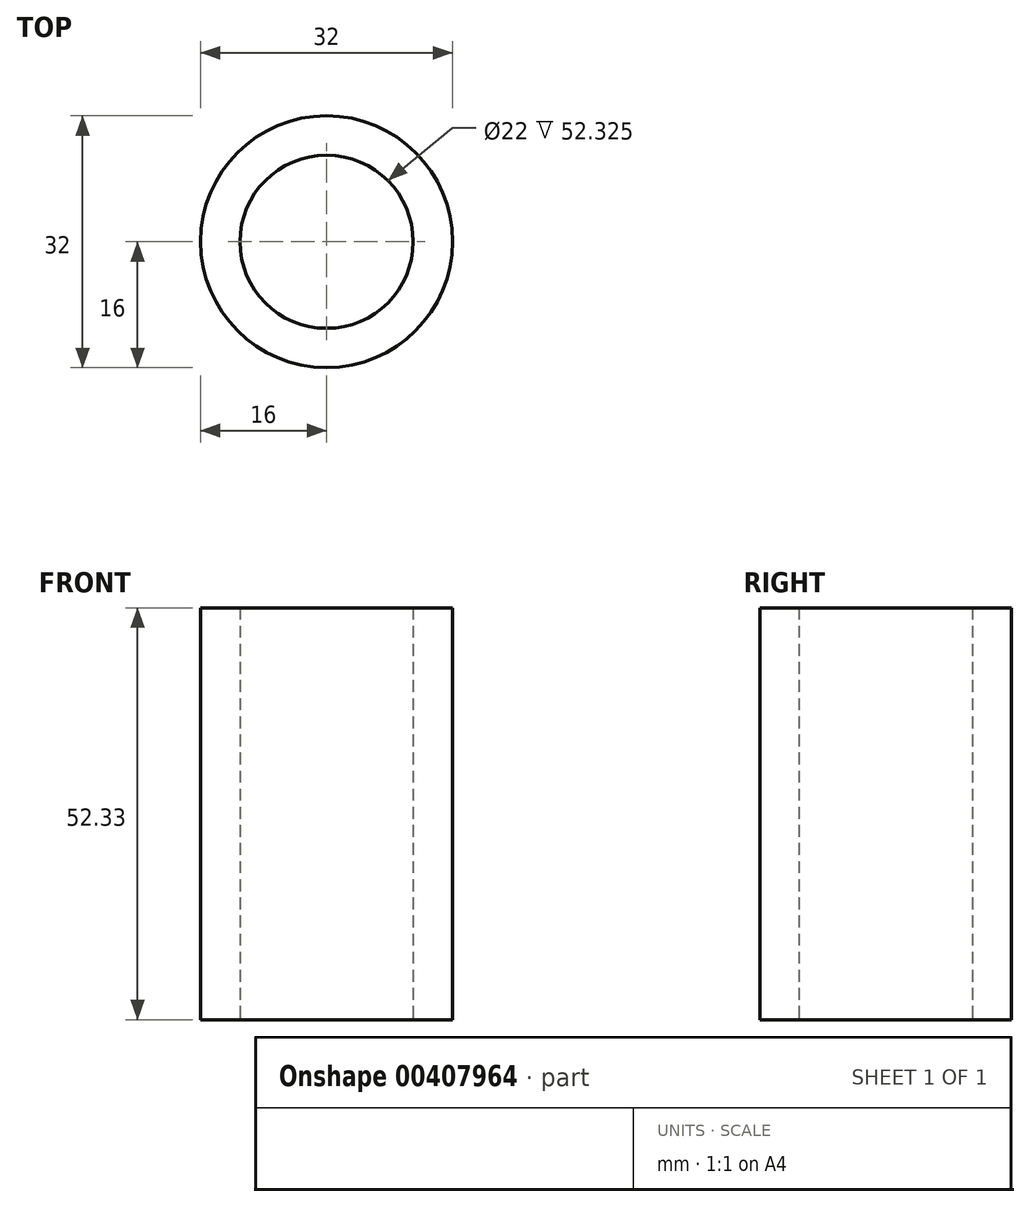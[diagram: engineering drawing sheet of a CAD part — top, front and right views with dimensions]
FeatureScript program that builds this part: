
annotation { "Feature Type Name" : "Feature", "Feature Type Description" : "" }
export const myFeature = defineFeature(function(context is Context, id is Id, definition is map)
    precondition{}
    {
        {
            var Q0;
            Q0=qCreatedBy(makeId("Top.planeOp"),FACE);
            var sketch = newSketch(context, id + "F0", { "sketchPlane" : qUnion([Q0])});
            skCircle(sketch, "E0", {"center": v(0, 0) * mm, "radius": 16 * mm});
            skCircle(sketch, "E1", {"center": v(0, 0) * mm, "radius": 11 * mm});
            skSolve(sketch);
        }
        {
            var Q0;
            Q0=makeQuery(id+"F0.imprint","IMPRINT",FACE,{"disambiguationData":[TD([[makeQuery(id+"F0.imprint","IMPRINT",EDGE,{"derivedFrom":sQuery(id+"F0.wireOp",EDGE,"E0")}),1.0]])]});
            extrude(context, id + "F1", {"entities" : qUnion([Q0]), "depth" : 52.33 * mm});
        }
    });
